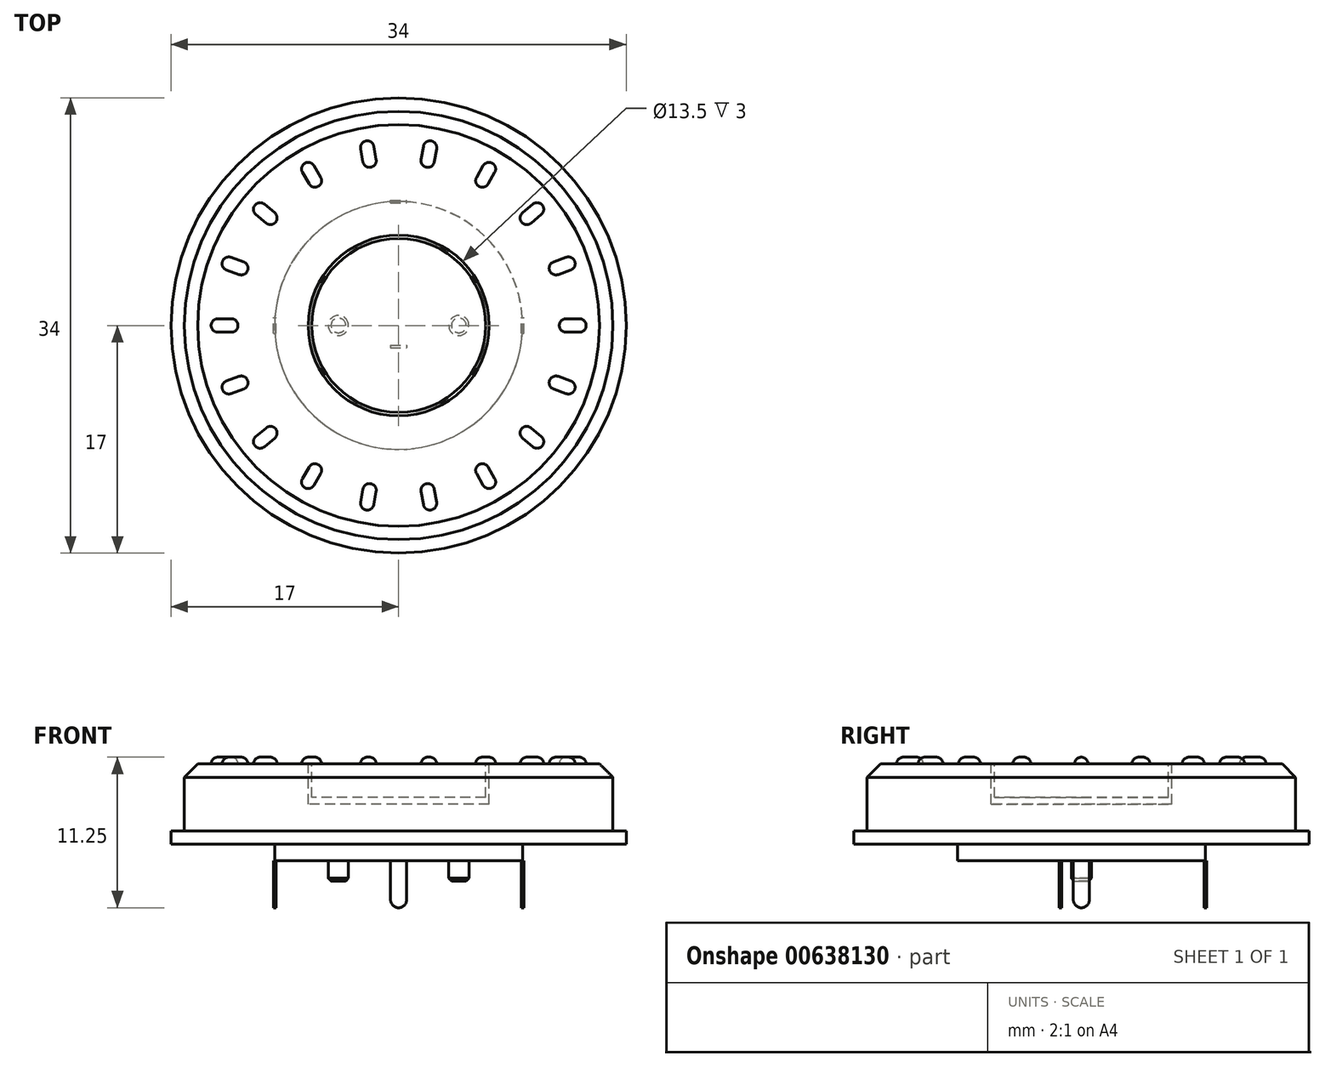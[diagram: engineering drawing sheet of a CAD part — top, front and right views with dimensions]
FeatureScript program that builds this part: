
annotation { "Feature Type Name" : "Feature", "Feature Type Description" : "" }
export const myFeature = defineFeature(function(context is Context, id is Id, definition is map)
    precondition{}
    {
        {
            var Q0;
            Q0=qCreatedBy(makeId("Top.planeOp"),FACE);
            var sketch = newSketch(context, id + "F0", { "sketchPlane" : qUnion([Q0])});
            skCircle(sketch, "E0", {"center": v(0, 0) * mm, "radius": 17 * mm});
            skSolve(sketch);
        }
        {
            var Q0;
            Q0 = qSketchRegion(id + "F0", true);
            extrude(context, id + "F1", {"entities" : qUnion([Q0]), "depth" : 1 * mm, "offsetDistance" : 25 * mm});
        }
        {
            var Q0;
            Q0=makeQuery(id+"F1.opExtrude","CAP_FACE",FACE,{"disambiguationData":[OSD([sQuery(id+"F0.wireOp",EDGE,"E0")])],"isStart":false});
            var sketch = newSketch(context, id + "F2", { "sketchPlane" : qUnion([Q0])});
            skCircle(sketch, "E1", {"center": v(0, 0) * mm, "radius": 16 * mm});
            skSolve(sketch);
        }
        {
            var Q0;
            Q0 = qSketchRegion(id + "F2", true);
            extrude(context, id + "F3", {"entities" : qUnion([Q0]), "operationType" : NewBodyOperationType.ADD, "depth" : 5 * mm, "offsetDistance" : 25 * mm});
        }
        {
            var Q0;
            Q0=makeQuery(id+"F3.opExtrude","CAP_EDGE",EDGE,{"disambiguationData":[OSD([sQuery(id+"F2.wireOp",EDGE,"E1")])],"isStart":false});
            chamfer(context, id + "F4", {"entities" : qUnion([Q0]), "width" : 1 * mm, "tangentPropagation" : true});
        }
        {
            var Q0;
            Q0=makeQuery(id+"F3.opExtrude","CAP_FACE",FACE,{"disambiguationData":[OSD([sQuery(id+"F2.wireOp",EDGE,"E1")])],"isStart":false});
            var sketch = newSketch(context, id + "F5", { "sketchPlane" : qUnion([Q0])});
            skCircle(sketch, "E2", {"center": v(0, 0) * mm, "radius": 6.75 * mm});
            skSolve(sketch);
        }
        {
            var Q0;
            Q0 = qSketchRegion(id + "F5", true);
            extrude(context, id + "F6", {"entities" : qUnion([Q0]), "operationType" : NewBodyOperationType.REMOVE, "oppositeDirection" : true, "depth" : 3 * mm, "offsetDistance" : 25 * mm});
        }
        {
            var Q0;
            Q0=makeQuery(id+"F3.opExtrude","CAP_FACE",FACE,{"disambiguationData":[OSD([sQuery(id+"F2.wireOp",EDGE,"E1")])],"isStart":false});
            var sketch = newSketch(context, id + "F7", { "sketchPlane" : qUnion([Q0])});
            skCircle(sketch, "E3", {"center": v(0, 0) * mm, "radius": 6.5 * mm});
            skSolve(sketch);
        }
        {
            var Q0;
            Q0 = qSketchRegion(id + "F7", true);
            extrude(context, id + "F8", {"entities" : qUnion([Q0]), "oppositeDirection" : true, "depth" : 2.5 * mm, "offsetDistance" : 25 * mm});
        }
        {
            var Q0;
            Q0=makeQuery(id+"F3.opExtrude","CAP_FACE",FACE,{"disambiguationData":[OSD([sQuery(id+"F2.wireOp",EDGE,"E1")])],"isStart":false});
            var sketch = newSketch(context, id + "F9", { "sketchPlane" : qUnion([Q0])});
            skLineSegment(sketch, "E4.bottom", {"start": v(12, 0.5) * mm, "end": v(14, 0.5) * mm});
            skLineSegment(sketch, "E4.top", {"start": v(12, -0.5) * mm, "end": v(14, -0.5) * mm});
            skLineSegment(sketch, "E4.left", {"start": v(12, 0.5) * mm, "end": v(12, -0.5) * mm});
            skLineSegment(sketch, "E4.right", {"start": v(14, 0.5) * mm, "end": v(14, -0.5) * mm});
            skLineSegment(sketch, "E5.1.0", {"start": v(11.1, 4.57) * mm, "end": v(12.98, 5.26) * mm});
            skLineSegment(sketch, "E5.1.1", {"start": v(11.1, 4.57) * mm, "end": v(11.45, 3.63) * mm});
            skLineSegment(sketch, "E5.1.2", {"start": v(11.45, 3.63) * mm, "end": v(13.33, 4.32) * mm});
            skLineSegment(sketch, "E5.1.3", {"start": v(12.98, 5.26) * mm, "end": v(13.33, 4.32) * mm});
            skLineSegment(sketch, "E5.2.0", {"start": v(8.87, 8.1) * mm, "end": v(10.4, 9.38) * mm});
            skLineSegment(sketch, "E5.2.1", {"start": v(8.87, 8.1) * mm, "end": v(9.51, 7.33) * mm});
            skLineSegment(sketch, "E5.2.2", {"start": v(9.51, 7.33) * mm, "end": v(11.05, 8.62) * mm});
            skLineSegment(sketch, "E5.2.3", {"start": v(10.4, 9.38) * mm, "end": v(11.05, 8.62) * mm});
            skLineSegment(sketch, "E5.3.0", {"start": v(5.57, 10.64) * mm, "end": v(6.57, 12.37) * mm});
            skLineSegment(sketch, "E5.3.1", {"start": v(5.57, 10.64) * mm, "end": v(6.43, 10.14) * mm});
            skLineSegment(sketch, "E5.3.2", {"start": v(6.43, 10.14) * mm, "end": v(7.43, 11.87) * mm});
            skLineSegment(sketch, "E5.3.3", {"start": v(6.57, 12.37) * mm, "end": v(7.43, 11.87) * mm});
            skLineSegment(sketch, "E5.4.0", {"start": v(1.6, 11.9) * mm, "end": v(1.94, 13.87) * mm});
            skLineSegment(sketch, "E5.4.1", {"start": v(1.6, 11.9) * mm, "end": v(2.58, 11.73) * mm});
            skLineSegment(sketch, "E5.4.2", {"start": v(2.58, 11.73) * mm, "end": v(2.92, 13.7) * mm});
            skLineSegment(sketch, "E5.4.3", {"start": v(1.94, 13.87) * mm, "end": v(2.92, 13.7) * mm});
            skLineSegment(sketch, "E5.5.0", {"start": v(-2.58, 11.73) * mm, "end": v(-2.92, 13.7) * mm});
            skLineSegment(sketch, "E5.5.1", {"start": v(-2.58, 11.73) * mm, "end": v(-1.6, 11.9) * mm});
            skLineSegment(sketch, "E5.5.2", {"start": v(-1.6, 11.9) * mm, "end": v(-1.94, 13.87) * mm});
            skLineSegment(sketch, "E5.5.3", {"start": v(-2.92, 13.7) * mm, "end": v(-1.94, 13.87) * mm});
            skLineSegment(sketch, "E5.6.0", {"start": v(-6.43, 10.14) * mm, "end": v(-7.43, 11.87) * mm});
            skLineSegment(sketch, "E5.6.1", {"start": v(-6.43, 10.14) * mm, "end": v(-5.57, 10.64) * mm});
            skLineSegment(sketch, "E5.6.2", {"start": v(-5.57, 10.64) * mm, "end": v(-6.57, 12.37) * mm});
            skLineSegment(sketch, "E5.6.3", {"start": v(-7.43, 11.87) * mm, "end": v(-6.57, 12.37) * mm});
            skLineSegment(sketch, "E5.7.0", {"start": v(-9.51, 7.33) * mm, "end": v(-11.05, 8.62) * mm});
            skLineSegment(sketch, "E5.7.1", {"start": v(-9.51, 7.33) * mm, "end": v(-8.87, 8.1) * mm});
            skLineSegment(sketch, "E5.7.2", {"start": v(-8.87, 8.1) * mm, "end": v(-10.4, 9.38) * mm});
            skLineSegment(sketch, "E5.7.3", {"start": v(-11.05, 8.62) * mm, "end": v(-10.4, 9.38) * mm});
            skLineSegment(sketch, "E5.8.0", {"start": v(-11.45, 3.63) * mm, "end": v(-13.33, 4.32) * mm});
            skLineSegment(sketch, "E5.8.1", {"start": v(-11.45, 3.63) * mm, "end": v(-11.1, 4.57) * mm});
            skLineSegment(sketch, "E5.8.2", {"start": v(-11.1, 4.57) * mm, "end": v(-12.98, 5.26) * mm});
            skLineSegment(sketch, "E5.8.3", {"start": v(-13.33, 4.32) * mm, "end": v(-12.98, 5.26) * mm});
            skLineSegment(sketch, "E5.9.0", {"start": v(-12, -0.5) * mm, "end": v(-14, -0.5) * mm});
            skLineSegment(sketch, "E5.9.1", {"start": v(-12, -0.5) * mm, "end": v(-12, 0.5) * mm});
            skLineSegment(sketch, "E5.9.2", {"start": v(-12, 0.5) * mm, "end": v(-14, 0.5) * mm});
            skLineSegment(sketch, "E5.9.3", {"start": v(-14, -0.5) * mm, "end": v(-14, 0.5) * mm});
            skLineSegment(sketch, "E5.10.0", {"start": v(-11.1, -4.57) * mm, "end": v(-12.98, -5.26) * mm});
            skLineSegment(sketch, "E5.10.1", {"start": v(-11.1, -4.57) * mm, "end": v(-11.45, -3.63) * mm});
            skLineSegment(sketch, "E5.10.2", {"start": v(-11.45, -3.63) * mm, "end": v(-13.33, -4.32) * mm});
            skLineSegment(sketch, "E5.10.3", {"start": v(-12.98, -5.26) * mm, "end": v(-13.33, -4.32) * mm});
            skLineSegment(sketch, "E5.11.0", {"start": v(-8.87, -8.1) * mm, "end": v(-10.4, -9.38) * mm});
            skLineSegment(sketch, "E5.11.1", {"start": v(-8.87, -8.1) * mm, "end": v(-9.51, -7.33) * mm});
            skLineSegment(sketch, "E5.11.2", {"start": v(-9.51, -7.33) * mm, "end": v(-11.05, -8.62) * mm});
            skLineSegment(sketch, "E5.11.3", {"start": v(-10.4, -9.38) * mm, "end": v(-11.05, -8.62) * mm});
            skLineSegment(sketch, "E5.12.0", {"start": v(-5.57, -10.64) * mm, "end": v(-6.57, -12.37) * mm});
            skLineSegment(sketch, "E5.12.1", {"start": v(-5.57, -10.64) * mm, "end": v(-6.43, -10.14) * mm});
            skLineSegment(sketch, "E5.12.2", {"start": v(-6.43, -10.14) * mm, "end": v(-7.43, -11.87) * mm});
            skLineSegment(sketch, "E5.12.3", {"start": v(-6.57, -12.37) * mm, "end": v(-7.43, -11.87) * mm});
            skLineSegment(sketch, "E5.13.0", {"start": v(-1.6, -11.9) * mm, "end": v(-1.94, -13.87) * mm});
            skLineSegment(sketch, "E5.13.1", {"start": v(-1.6, -11.9) * mm, "end": v(-2.58, -11.73) * mm});
            skLineSegment(sketch, "E5.13.2", {"start": v(-2.58, -11.73) * mm, "end": v(-2.92, -13.7) * mm});
            skLineSegment(sketch, "E5.13.3", {"start": v(-1.94, -13.87) * mm, "end": v(-2.92, -13.7) * mm});
            skLineSegment(sketch, "E5.14.0", {"start": v(2.58, -11.73) * mm, "end": v(2.92, -13.7) * mm});
            skLineSegment(sketch, "E5.14.1", {"start": v(2.58, -11.73) * mm, "end": v(1.6, -11.9) * mm});
            skLineSegment(sketch, "E5.14.2", {"start": v(1.6, -11.9) * mm, "end": v(1.94, -13.87) * mm});
            skLineSegment(sketch, "E5.14.3", {"start": v(2.92, -13.7) * mm, "end": v(1.94, -13.87) * mm});
            skLineSegment(sketch, "E5.15.0", {"start": v(6.43, -10.14) * mm, "end": v(7.43, -11.87) * mm});
            skLineSegment(sketch, "E5.15.1", {"start": v(6.43, -10.14) * mm, "end": v(5.57, -10.64) * mm});
            skLineSegment(sketch, "E5.15.2", {"start": v(5.57, -10.64) * mm, "end": v(6.57, -12.37) * mm});
            skLineSegment(sketch, "E5.15.3", {"start": v(7.43, -11.87) * mm, "end": v(6.57, -12.37) * mm});
            skLineSegment(sketch, "E5.16.0", {"start": v(9.51, -7.33) * mm, "end": v(11.05, -8.62) * mm});
            skLineSegment(sketch, "E5.16.1", {"start": v(9.51, -7.33) * mm, "end": v(8.87, -8.1) * mm});
            skLineSegment(sketch, "E5.16.2", {"start": v(8.87, -8.1) * mm, "end": v(10.4, -9.38) * mm});
            skLineSegment(sketch, "E5.16.3", {"start": v(11.05, -8.62) * mm, "end": v(10.4, -9.38) * mm});
            skLineSegment(sketch, "E5.17.0", {"start": v(11.45, -3.63) * mm, "end": v(13.33, -4.32) * mm});
            skLineSegment(sketch, "E5.17.1", {"start": v(11.45, -3.63) * mm, "end": v(11.1, -4.57) * mm});
            skLineSegment(sketch, "E5.17.2", {"start": v(11.1, -4.57) * mm, "end": v(12.98, -5.26) * mm});
            skLineSegment(sketch, "E5.17.3", {"start": v(13.33, -4.32) * mm, "end": v(12.98, -5.26) * mm});
            skPoint(sketch, "E5.center", {"position": v(0, 0) * mm});
            skSolve(sketch);
        }
        {
            var Q0;
            Q0=makeQuery(id+"F9.imprint","IMPRINT",FACE,{"disambiguationData":[TD([[makeQuery(id+"F9.imprint","IMPRINT",EDGE,{"derivedFrom":sQuery(id+"F9.wireOp",EDGE,"E4.bottom")}),-1.0]])]});
            var Q1;
            Q1=makeQuery(id+"F9.imprint","IMPRINT",FACE,{"disambiguationData":[TD([[makeQuery(id+"F9.imprint","IMPRINT",EDGE,{"derivedFrom":sQuery(id+"F9.wireOp",EDGE,"E5.1.0")}),-1.0]])]});
            var Q2;
            Q2=makeQuery(id+"F9.imprint","IMPRINT",FACE,{"disambiguationData":[TD([[makeQuery(id+"F9.imprint","IMPRINT",EDGE,{"derivedFrom":sQuery(id+"F9.wireOp",EDGE,"E5.2.0")}),-1.0]])]});
            var Q3;
            Q3=makeQuery(id+"F9.imprint","IMPRINT",FACE,{"disambiguationData":[TD([[makeQuery(id+"F9.imprint","IMPRINT",EDGE,{"derivedFrom":sQuery(id+"F9.wireOp",EDGE,"E5.3.0")}),-1.0]])]});
            var Q4;
            Q4=makeQuery(id+"F9.imprint","IMPRINT",FACE,{"disambiguationData":[TD([[makeQuery(id+"F9.imprint","IMPRINT",EDGE,{"derivedFrom":sQuery(id+"F9.wireOp",EDGE,"E5.4.0")}),-1.0]])]});
            var Q5;
            Q5=makeQuery(id+"F9.imprint","IMPRINT",FACE,{"disambiguationData":[TD([[makeQuery(id+"F9.imprint","IMPRINT",EDGE,{"derivedFrom":sQuery(id+"F9.wireOp",EDGE,"E5.5.0")}),-1.0]])]});
            var Q6;
            Q6=makeQuery(id+"F9.imprint","IMPRINT",FACE,{"disambiguationData":[TD([[makeQuery(id+"F9.imprint","IMPRINT",EDGE,{"derivedFrom":sQuery(id+"F9.wireOp",EDGE,"E5.6.0")}),-1.0]])]});
            var Q7;
            Q7=makeQuery(id+"F9.imprint","IMPRINT",FACE,{"disambiguationData":[TD([[makeQuery(id+"F9.imprint","IMPRINT",EDGE,{"derivedFrom":sQuery(id+"F9.wireOp",EDGE,"E5.7.0")}),-1.0]])]});
            var Q8;
            Q8=makeQuery(id+"F9.imprint","IMPRINT",FACE,{"disambiguationData":[TD([[makeQuery(id+"F9.imprint","IMPRINT",EDGE,{"derivedFrom":sQuery(id+"F9.wireOp",EDGE,"E5.8.0")}),-1.0]])]});
            var Q9;
            Q9=makeQuery(id+"F9.imprint","IMPRINT",FACE,{"disambiguationData":[TD([[makeQuery(id+"F9.imprint","IMPRINT",EDGE,{"derivedFrom":sQuery(id+"F9.wireOp",EDGE,"E5.9.0")}),-1.0]])]});
            var Q10;
            Q10=makeQuery(id+"F9.imprint","IMPRINT",FACE,{"disambiguationData":[TD([[makeQuery(id+"F9.imprint","IMPRINT",EDGE,{"derivedFrom":sQuery(id+"F9.wireOp",EDGE,"E5.10.0")}),-1.0]])]});
            var Q11;
            Q11=makeQuery(id+"F9.imprint","IMPRINT",FACE,{"disambiguationData":[TD([[makeQuery(id+"F9.imprint","IMPRINT",EDGE,{"derivedFrom":sQuery(id+"F9.wireOp",EDGE,"E5.11.0")}),-1.0]])]});
            var Q12;
            Q12=makeQuery(id+"F9.imprint","IMPRINT",FACE,{"disambiguationData":[TD([[makeQuery(id+"F9.imprint","IMPRINT",EDGE,{"derivedFrom":sQuery(id+"F9.wireOp",EDGE,"E5.12.0")}),-1.0]])]});
            var Q13;
            Q13=makeQuery(id+"F9.imprint","IMPRINT",FACE,{"disambiguationData":[TD([[makeQuery(id+"F9.imprint","IMPRINT",EDGE,{"derivedFrom":sQuery(id+"F9.wireOp",EDGE,"E5.13.0")}),-1.0]])]});
            var Q14;
            Q14=makeQuery(id+"F9.imprint","IMPRINT",FACE,{"disambiguationData":[TD([[makeQuery(id+"F9.imprint","IMPRINT",EDGE,{"derivedFrom":sQuery(id+"F9.wireOp",EDGE,"E5.14.0")}),-1.0]])]});
            var Q15;
            Q15=makeQuery(id+"F9.imprint","IMPRINT",FACE,{"disambiguationData":[TD([[makeQuery(id+"F9.imprint","IMPRINT",EDGE,{"derivedFrom":sQuery(id+"F9.wireOp",EDGE,"E5.15.0")}),-1.0]])]});
            var Q16;
            Q16=makeQuery(id+"F9.imprint","IMPRINT",FACE,{"disambiguationData":[TD([[makeQuery(id+"F9.imprint","IMPRINT",EDGE,{"derivedFrom":sQuery(id+"F9.wireOp",EDGE,"E5.16.0")}),-1.0]])]});
            var Q17;
            Q17=makeQuery(id+"F9.imprint","IMPRINT",FACE,{"disambiguationData":[TD([[makeQuery(id+"F9.imprint","IMPRINT",EDGE,{"derivedFrom":sQuery(id+"F9.wireOp",EDGE,"E5.17.0")}),-1.0]])]});
            extrude(context, id + "F10", {"entities" : qUnion([Q0, Q1, Q2, Q3, Q4, Q5, Q6, Q7, Q8, Q9, Q10, Q11, Q12, Q13, Q14, Q15, Q16, Q17]), "operationType" : NewBodyOperationType.ADD, "depth" : 0.5 * mm, "offsetDistance" : 25 * mm});
        }
        {
            var Q0;
            Q0=makeQuery(id+"F10.opExtrude","SWEPT_EDGE",EDGE,{"disambiguationData":[OSD([sQuery(id+"F9.wireOp",EDGE,"E4.top"),sQuery(id+"F9.wireOp",EDGE,"E4.right")])]});
            var Q1;
            Q1=makeQuery(id+"F10.opExtrude","SWEPT_EDGE",EDGE,{"disambiguationData":[OSD([sQuery(id+"F9.wireOp",EDGE,"E4.bottom"),sQuery(id+"F9.wireOp",EDGE,"E4.right")])]});
            var Q2;
            Q2=makeQuery(id+"F10.opExtrude","SWEPT_EDGE",EDGE,{"disambiguationData":[OSD([sQuery(id+"F9.wireOp",EDGE,"E4.top"),sQuery(id+"F9.wireOp",EDGE,"E4.left")])]});
            var Q3;
            Q3=makeQuery(id+"F10.opExtrude","SWEPT_EDGE",EDGE,{"disambiguationData":[OSD([sQuery(id+"F9.wireOp",EDGE,"E4.bottom"),sQuery(id+"F9.wireOp",EDGE,"E4.left")])]});
            var Q4;
            Q4=makeQuery(id+"F10.opExtrude","CAP_EDGE",EDGE,{"disambiguationData":[OSD([sQuery(id+"F9.wireOp",EDGE,"E4.bottom")])],"isStart":false});
            var Q5;
            Q5=makeQuery(id+"F10.opExtrude","CAP_EDGE",EDGE,{"disambiguationData":[OSD([sQuery(id+"F9.wireOp",EDGE,"E4.top")])],"isStart":false});
            var Q6;
            Q6=makeQuery(id+"F10.opExtrude","CAP_EDGE",EDGE,{"disambiguationData":[OSD([sQuery(id+"F9.wireOp",EDGE,"E4.left")])],"isStart":false});
            var Q7;
            Q7=makeQuery(id+"F10.opExtrude","CAP_EDGE",EDGE,{"disambiguationData":[OSD([sQuery(id+"F9.wireOp",EDGE,"E4.right")])],"isStart":false});
            fillet(context, id + "F11", {"entities" : qUnion([Q0, Q1, Q2, Q3, Q4, Q5, Q6, Q7]), "radius" : 0.5 * mm, "tangentPropagation" : true, "allowEdgeOverflow" : false});
        }
        {
            var Q0;
            Q0=makeQuery(id+"F10.opExtrude","SWEPT_EDGE",EDGE,{"disambiguationData":[OSD([sQuery(id+"F9.wireOp",EDGE,"E5.1.0"),sQuery(id+"F9.wireOp",EDGE,"E5.1.3")])]});
            var Q1;
            Q1=makeQuery(id+"F10.opExtrude","SWEPT_EDGE",EDGE,{"disambiguationData":[OSD([sQuery(id+"F9.wireOp",EDGE,"E5.1.2"),sQuery(id+"F9.wireOp",EDGE,"E5.1.3")])]});
            var Q2;
            Q2=makeQuery(id+"F10.opExtrude","SWEPT_EDGE",EDGE,{"disambiguationData":[OSD([sQuery(id+"F9.wireOp",EDGE,"E5.1.0"),sQuery(id+"F9.wireOp",EDGE,"E5.1.1")])]});
            var Q3;
            Q3=makeQuery(id+"F10.opExtrude","SWEPT_EDGE",EDGE,{"disambiguationData":[OSD([sQuery(id+"F9.wireOp",EDGE,"E5.1.1"),sQuery(id+"F9.wireOp",EDGE,"E5.1.2")])]});
            var Q4;
            Q4=makeQuery(id+"F10.opExtrude","CAP_EDGE",EDGE,{"disambiguationData":[OSD([sQuery(id+"F9.wireOp",EDGE,"E5.1.2")])],"isStart":false});
            var Q5;
            Q5=makeQuery(id+"F10.opExtrude","CAP_EDGE",EDGE,{"disambiguationData":[OSD([sQuery(id+"F9.wireOp",EDGE,"E5.1.0")])],"isStart":false});
            var Q6;
            Q6=makeQuery(id+"F10.opExtrude","CAP_EDGE",EDGE,{"disambiguationData":[OSD([sQuery(id+"F9.wireOp",EDGE,"E5.1.1")])],"isStart":false});
            var Q7;
            Q7=makeQuery(id+"F10.opExtrude","CAP_EDGE",EDGE,{"disambiguationData":[OSD([sQuery(id+"F9.wireOp",EDGE,"E5.1.3")])],"isStart":false});
            fillet(context, id + "F12", {"entities" : qUnion([Q0, Q1, Q2, Q3, Q4, Q5, Q6, Q7]), "radius" : 0.5 * mm, "tangentPropagation" : true, "allowEdgeOverflow" : false});
        }
        {
            var Q0;
            Q0=makeQuery(id+"F10.opExtrude","SWEPT_EDGE",EDGE,{"disambiguationData":[OSD([sQuery(id+"F9.wireOp",EDGE,"E5.17.2"),sQuery(id+"F9.wireOp",EDGE,"E5.17.3")])]});
            var Q1;
            Q1=makeQuery(id+"F10.opExtrude","SWEPT_EDGE",EDGE,{"disambiguationData":[OSD([sQuery(id+"F9.wireOp",EDGE,"E5.17.0"),sQuery(id+"F9.wireOp",EDGE,"E5.17.3")])]});
            var Q2;
            Q2=makeQuery(id+"F10.opExtrude","SWEPT_EDGE",EDGE,{"disambiguationData":[OSD([sQuery(id+"F9.wireOp",EDGE,"E5.17.1"),sQuery(id+"F9.wireOp",EDGE,"E5.17.2")])]});
            var Q3;
            Q3=makeQuery(id+"F10.opExtrude","SWEPT_EDGE",EDGE,{"disambiguationData":[OSD([sQuery(id+"F9.wireOp",EDGE,"E5.17.0"),sQuery(id+"F9.wireOp",EDGE,"E5.17.1")])]});
            var Q4;
            Q4=makeQuery(id+"F10.opExtrude","CAP_EDGE",EDGE,{"disambiguationData":[OSD([sQuery(id+"F9.wireOp",EDGE,"E5.17.0")])],"isStart":false});
            var Q5;
            Q5=makeQuery(id+"F10.opExtrude","CAP_EDGE",EDGE,{"disambiguationData":[OSD([sQuery(id+"F9.wireOp",EDGE,"E5.17.2")])],"isStart":false});
            var Q6;
            Q6=makeQuery(id+"F10.opExtrude","CAP_EDGE",EDGE,{"disambiguationData":[OSD([sQuery(id+"F9.wireOp",EDGE,"E5.17.3")])],"isStart":false});
            var Q7;
            Q7=makeQuery(id+"F10.opExtrude","CAP_FACE",FACE,{"disambiguationData":[OSD([sQuery(id+"F9.wireOp",EDGE,"E5.17.0"),sQuery(id+"F9.wireOp",EDGE,"E5.17.1"),sQuery(id+"F9.wireOp",EDGE,"E5.17.2"),sQuery(id+"F9.wireOp",EDGE,"E5.17.3")])],"isStart":false});
            fillet(context, id + "F13", {"entities" : qUnion([Q0, Q1, Q2, Q3, Q4, Q5, Q6, Q7]), "radius" : 0.5 * mm, "tangentPropagation" : true, "allowEdgeOverflow" : false});
        }
        {
            var Q0;
            Q0=makeQuery(id+"F10.opExtrude","SWEPT_EDGE",EDGE,{"disambiguationData":[OSD([sQuery(id+"F9.wireOp",EDGE,"E5.16.2"),sQuery(id+"F9.wireOp",EDGE,"E5.16.3")])]});
            var Q1;
            Q1=makeQuery(id+"F10.opExtrude","SWEPT_EDGE",EDGE,{"disambiguationData":[OSD([sQuery(id+"F9.wireOp",EDGE,"E5.16.0"),sQuery(id+"F9.wireOp",EDGE,"E5.16.3")])]});
            var Q2;
            Q2=makeQuery(id+"F10.opExtrude","SWEPT_EDGE",EDGE,{"disambiguationData":[OSD([sQuery(id+"F9.wireOp",EDGE,"E5.16.1"),sQuery(id+"F9.wireOp",EDGE,"E5.16.2")])]});
            var Q3;
            Q3=makeQuery(id+"F10.opExtrude","SWEPT_EDGE",EDGE,{"disambiguationData":[OSD([sQuery(id+"F9.wireOp",EDGE,"E5.16.0"),sQuery(id+"F9.wireOp",EDGE,"E5.16.1")])]});
            var Q4;
            Q4=makeQuery(id+"F10.opExtrude","CAP_EDGE",EDGE,{"disambiguationData":[OSD([sQuery(id+"F9.wireOp",EDGE,"E5.16.0")])],"isStart":false});
            var Q5;
            Q5=makeQuery(id+"F10.opExtrude","CAP_EDGE",EDGE,{"disambiguationData":[OSD([sQuery(id+"F9.wireOp",EDGE,"E5.16.2")])],"isStart":false});
            var Q6;
            Q6=makeQuery(id+"F10.opExtrude","CAP_EDGE",EDGE,{"disambiguationData":[OSD([sQuery(id+"F9.wireOp",EDGE,"E5.16.3")])],"isStart":false});
            var Q7;
            Q7=makeQuery(id+"F10.opExtrude","CAP_EDGE",EDGE,{"disambiguationData":[OSD([sQuery(id+"F9.wireOp",EDGE,"E5.16.1")])],"isStart":false});
            fillet(context, id + "F14", {"entities" : qUnion([Q0, Q1, Q2, Q3, Q4, Q5, Q6, Q7]), "radius" : 0.5 * mm, "tangentPropagation" : true, "allowEdgeOverflow" : false});
        }
        {
            var Q0;
            Q0=makeQuery(id+"F10.opExtrude","SWEPT_EDGE",EDGE,{"disambiguationData":[OSD([sQuery(id+"F9.wireOp",EDGE,"E5.15.0"),sQuery(id+"F9.wireOp",EDGE,"E5.15.3")])]});
            var Q1;
            Q1=makeQuery(id+"F10.opExtrude","SWEPT_EDGE",EDGE,{"disambiguationData":[OSD([sQuery(id+"F9.wireOp",EDGE,"E5.15.0"),sQuery(id+"F9.wireOp",EDGE,"E5.15.1")])]});
            var Q2;
            Q2=makeQuery(id+"F10.opExtrude","SWEPT_EDGE",EDGE,{"disambiguationData":[OSD([sQuery(id+"F9.wireOp",EDGE,"E5.15.2"),sQuery(id+"F9.wireOp",EDGE,"E5.15.3")])]});
            var Q3;
            Q3=makeQuery(id+"F10.opExtrude","SWEPT_EDGE",EDGE,{"disambiguationData":[OSD([sQuery(id+"F9.wireOp",EDGE,"E5.15.1"),sQuery(id+"F9.wireOp",EDGE,"E5.15.2")])]});
            var Q4;
            Q4=makeQuery(id+"F10.opExtrude","CAP_EDGE",EDGE,{"disambiguationData":[OSD([sQuery(id+"F9.wireOp",EDGE,"E5.15.2")])],"isStart":false});
            var Q5;
            Q5=makeQuery(id+"F10.opExtrude","CAP_EDGE",EDGE,{"disambiguationData":[OSD([sQuery(id+"F9.wireOp",EDGE,"E5.15.0")])],"isStart":false});
            var Q6;
            Q6=makeQuery(id+"F10.opExtrude","CAP_EDGE",EDGE,{"disambiguationData":[OSD([sQuery(id+"F9.wireOp",EDGE,"E5.15.3")])],"isStart":false});
            var Q7;
            Q7=makeQuery(id+"F10.opExtrude","CAP_EDGE",EDGE,{"disambiguationData":[OSD([sQuery(id+"F9.wireOp",EDGE,"E5.15.1")])],"isStart":false});
            fillet(context, id + "F15", {"entities" : qUnion([Q0, Q1, Q2, Q3, Q4, Q5, Q6, Q7]), "radius" : 0.5 * mm, "tangentPropagation" : true, "allowEdgeOverflow" : false});
        }
        {
            var Q0;
            Q0=makeQuery(id+"F10.opExtrude","SWEPT_EDGE",EDGE,{"disambiguationData":[OSD([sQuery(id+"F9.wireOp",EDGE,"E5.14.1"),sQuery(id+"F9.wireOp",EDGE,"E5.14.2")])]});
            var Q1;
            Q1=makeQuery(id+"F10.opExtrude","SWEPT_EDGE",EDGE,{"disambiguationData":[OSD([sQuery(id+"F9.wireOp",EDGE,"E5.14.2"),sQuery(id+"F9.wireOp",EDGE,"E5.14.3")])]});
            var Q2;
            Q2=makeQuery(id+"F10.opExtrude","SWEPT_EDGE",EDGE,{"disambiguationData":[OSD([sQuery(id+"F9.wireOp",EDGE,"E5.14.0"),sQuery(id+"F9.wireOp",EDGE,"E5.14.3")])]});
            var Q3;
            Q3=makeQuery(id+"F10.opExtrude","SWEPT_EDGE",EDGE,{"disambiguationData":[OSD([sQuery(id+"F9.wireOp",EDGE,"E5.14.0"),sQuery(id+"F9.wireOp",EDGE,"E5.14.1")])]});
            var Q4;
            Q4=makeQuery(id+"F10.opExtrude","CAP_EDGE",EDGE,{"disambiguationData":[OSD([sQuery(id+"F9.wireOp",EDGE,"E5.14.2")])],"isStart":false});
            var Q5;
            Q5=makeQuery(id+"F10.opExtrude","CAP_EDGE",EDGE,{"disambiguationData":[OSD([sQuery(id+"F9.wireOp",EDGE,"E5.14.0")])],"isStart":false});
            var Q6;
            Q6=makeQuery(id+"F10.opExtrude","CAP_EDGE",EDGE,{"disambiguationData":[OSD([sQuery(id+"F9.wireOp",EDGE,"E5.14.3")])],"isStart":false});
            var Q7;
            Q7=makeQuery(id+"F10.opExtrude","CAP_EDGE",EDGE,{"disambiguationData":[OSD([sQuery(id+"F9.wireOp",EDGE,"E5.14.1")])],"isStart":false});
            fillet(context, id + "F16", {"entities" : qUnion([Q0, Q1, Q2, Q3, Q4, Q5, Q6, Q7]), "radius" : 0.5 * mm, "tangentPropagation" : true, "allowEdgeOverflow" : false});
        }
        {
            var Q0;
            Q0=makeQuery(id+"F10.opExtrude","SWEPT_EDGE",EDGE,{"disambiguationData":[OSD([sQuery(id+"F9.wireOp",EDGE,"E5.13.2"),sQuery(id+"F9.wireOp",EDGE,"E5.13.3")])]});
            var Q1;
            Q1=makeQuery(id+"F10.opExtrude","SWEPT_EDGE",EDGE,{"disambiguationData":[OSD([sQuery(id+"F9.wireOp",EDGE,"E5.13.0"),sQuery(id+"F9.wireOp",EDGE,"E5.13.3")])]});
            var Q2;
            Q2=makeQuery(id+"F10.opExtrude","SWEPT_EDGE",EDGE,{"disambiguationData":[OSD([sQuery(id+"F9.wireOp",EDGE,"E5.13.1"),sQuery(id+"F9.wireOp",EDGE,"E5.13.2")])]});
            var Q3;
            Q3=makeQuery(id+"F10.opExtrude","SWEPT_EDGE",EDGE,{"disambiguationData":[OSD([sQuery(id+"F9.wireOp",EDGE,"E5.13.0"),sQuery(id+"F9.wireOp",EDGE,"E5.13.1")])]});
            var Q4;
            Q4=makeQuery(id+"F10.opExtrude","CAP_EDGE",EDGE,{"disambiguationData":[OSD([sQuery(id+"F9.wireOp",EDGE,"E5.13.0")])],"isStart":false});
            var Q5;
            Q5=makeQuery(id+"F10.opExtrude","CAP_EDGE",EDGE,{"disambiguationData":[OSD([sQuery(id+"F9.wireOp",EDGE,"E5.13.2")])],"isStart":false});
            var Q6;
            Q6=makeQuery(id+"F10.opExtrude","CAP_EDGE",EDGE,{"disambiguationData":[OSD([sQuery(id+"F9.wireOp",EDGE,"E5.13.3")])],"isStart":false});
            var Q7;
            Q7=makeQuery(id+"F10.opExtrude","CAP_EDGE",EDGE,{"disambiguationData":[OSD([sQuery(id+"F9.wireOp",EDGE,"E5.13.1")])],"isStart":false});
            fillet(context, id + "F17", {"entities" : qUnion([Q0, Q1, Q2, Q3, Q4, Q5, Q6, Q7]), "radius" : 0.5 * mm, "tangentPropagation" : true, "allowEdgeOverflow" : false});
        }
        {
            var Q0;
            Q0=makeQuery(id+"F10.opExtrude","SWEPT_EDGE",EDGE,{"disambiguationData":[OSD([sQuery(id+"F9.wireOp",EDGE,"E5.12.2"),sQuery(id+"F9.wireOp",EDGE,"E5.12.3")])]});
            var Q1;
            Q1=makeQuery(id+"F10.opExtrude","SWEPT_EDGE",EDGE,{"disambiguationData":[OSD([sQuery(id+"F9.wireOp",EDGE,"E5.12.0"),sQuery(id+"F9.wireOp",EDGE,"E5.12.3")])]});
            var Q2;
            Q2=makeQuery(id+"F10.opExtrude","SWEPT_EDGE",EDGE,{"disambiguationData":[OSD([sQuery(id+"F9.wireOp",EDGE,"E5.12.1"),sQuery(id+"F9.wireOp",EDGE,"E5.12.2")])]});
            var Q3;
            Q3=makeQuery(id+"F10.opExtrude","SWEPT_EDGE",EDGE,{"disambiguationData":[OSD([sQuery(id+"F9.wireOp",EDGE,"E5.12.0"),sQuery(id+"F9.wireOp",EDGE,"E5.12.1")])]});
            var Q4;
            Q4=makeQuery(id+"F10.opExtrude","CAP_EDGE",EDGE,{"disambiguationData":[OSD([sQuery(id+"F9.wireOp",EDGE,"E5.12.2")])],"isStart":false});
            var Q5;
            Q5=makeQuery(id+"F10.opExtrude","CAP_EDGE",EDGE,{"disambiguationData":[OSD([sQuery(id+"F9.wireOp",EDGE,"E5.12.0")])],"isStart":false});
            var Q6;
            Q6=makeQuery(id+"F10.opExtrude","CAP_EDGE",EDGE,{"disambiguationData":[OSD([sQuery(id+"F9.wireOp",EDGE,"E5.12.3")])],"isStart":false});
            var Q7;
            Q7=makeQuery(id+"F10.opExtrude","CAP_EDGE",EDGE,{"disambiguationData":[OSD([sQuery(id+"F9.wireOp",EDGE,"E5.12.1")])],"isStart":false});
            fillet(context, id + "F18", {"entities" : qUnion([Q0, Q1, Q2, Q3, Q4, Q5, Q6, Q7]), "radius" : 0.5 * mm, "tangentPropagation" : true, "allowEdgeOverflow" : false});
        }
        {
            var Q0;
            Q0=makeQuery(id+"F10.opExtrude","SWEPT_EDGE",EDGE,{"disambiguationData":[OSD([sQuery(id+"F9.wireOp",EDGE,"E5.11.2"),sQuery(id+"F9.wireOp",EDGE,"E5.11.3")])]});
            var Q1;
            Q1=makeQuery(id+"F10.opExtrude","SWEPT_EDGE",EDGE,{"disambiguationData":[OSD([sQuery(id+"F9.wireOp",EDGE,"E5.11.0"),sQuery(id+"F9.wireOp",EDGE,"E5.11.3")])]});
            var Q2;
            Q2=makeQuery(id+"F10.opExtrude","SWEPT_EDGE",EDGE,{"disambiguationData":[OSD([sQuery(id+"F9.wireOp",EDGE,"E5.11.1"),sQuery(id+"F9.wireOp",EDGE,"E5.11.2")])]});
            var Q3;
            Q3=makeQuery(id+"F10.opExtrude","SWEPT_EDGE",EDGE,{"disambiguationData":[OSD([sQuery(id+"F9.wireOp",EDGE,"E5.11.0"),sQuery(id+"F9.wireOp",EDGE,"E5.11.1")])]});
            var Q4;
            Q4=makeQuery(id+"F10.opExtrude","CAP_EDGE",EDGE,{"disambiguationData":[OSD([sQuery(id+"F9.wireOp",EDGE,"E5.11.0")])],"isStart":false});
            var Q5;
            Q5=makeQuery(id+"F10.opExtrude","CAP_EDGE",EDGE,{"disambiguationData":[OSD([sQuery(id+"F9.wireOp",EDGE,"E5.11.2")])],"isStart":false});
            var Q6;
            Q6=makeQuery(id+"F10.opExtrude","CAP_EDGE",EDGE,{"disambiguationData":[OSD([sQuery(id+"F9.wireOp",EDGE,"E5.11.1")])],"isStart":false});
            var Q7;
            Q7=makeQuery(id+"F10.opExtrude","CAP_EDGE",EDGE,{"disambiguationData":[OSD([sQuery(id+"F9.wireOp",EDGE,"E5.11.3")])],"isStart":false});
            fillet(context, id + "F19", {"entities" : qUnion([Q0, Q1, Q2, Q3, Q4, Q5, Q6, Q7]), "radius" : 0.5 * mm, "tangentPropagation" : true, "allowEdgeOverflow" : false});
        }
        {
            var Q0;
            Q0=makeQuery(id+"F10.opExtrude","SWEPT_EDGE",EDGE,{"disambiguationData":[OSD([sQuery(id+"F9.wireOp",EDGE,"E5.10.2"),sQuery(id+"F9.wireOp",EDGE,"E5.10.3")])]});
            var Q1;
            Q1=makeQuery(id+"F10.opExtrude","SWEPT_EDGE",EDGE,{"disambiguationData":[OSD([sQuery(id+"F9.wireOp",EDGE,"E5.10.0"),sQuery(id+"F9.wireOp",EDGE,"E5.10.3")])]});
            var Q2;
            Q2=makeQuery(id+"F10.opExtrude","SWEPT_EDGE",EDGE,{"disambiguationData":[OSD([sQuery(id+"F9.wireOp",EDGE,"E5.10.1"),sQuery(id+"F9.wireOp",EDGE,"E5.10.2")])]});
            var Q3;
            Q3=makeQuery(id+"F10.opExtrude","SWEPT_EDGE",EDGE,{"disambiguationData":[OSD([sQuery(id+"F9.wireOp",EDGE,"E5.10.0"),sQuery(id+"F9.wireOp",EDGE,"E5.10.1")])]});
            var Q4;
            Q4=makeQuery(id+"F10.opExtrude","CAP_EDGE",EDGE,{"disambiguationData":[OSD([sQuery(id+"F9.wireOp",EDGE,"E5.10.0")])],"isStart":false});
            var Q5;
            Q5=makeQuery(id+"F10.opExtrude","CAP_EDGE",EDGE,{"disambiguationData":[OSD([sQuery(id+"F9.wireOp",EDGE,"E5.10.2")])],"isStart":false});
            var Q6;
            Q6=makeQuery(id+"F10.opExtrude","CAP_EDGE",EDGE,{"disambiguationData":[OSD([sQuery(id+"F9.wireOp",EDGE,"E5.10.1")])],"isStart":false});
            var Q7;
            Q7=makeQuery(id+"F10.opExtrude","CAP_EDGE",EDGE,{"disambiguationData":[OSD([sQuery(id+"F9.wireOp",EDGE,"E5.10.3")])],"isStart":false});
            fillet(context, id + "F20", {"entities" : qUnion([Q0, Q1, Q2, Q3, Q4, Q5, Q6, Q7]), "radius" : 0.5 * mm, "tangentPropagation" : true, "allowEdgeOverflow" : false});
        }
        {
            var Q0;
            Q0=makeQuery(id+"F10.opExtrude","SWEPT_EDGE",EDGE,{"disambiguationData":[OSD([sQuery(id+"F9.wireOp",EDGE,"E5.9.2"),sQuery(id+"F9.wireOp",EDGE,"E5.9.3")])]});
            var Q1;
            Q1=makeQuery(id+"F10.opExtrude","SWEPT_EDGE",EDGE,{"disambiguationData":[OSD([sQuery(id+"F9.wireOp",EDGE,"E5.9.0"),sQuery(id+"F9.wireOp",EDGE,"E5.9.3")])]});
            var Q2;
            Q2=makeQuery(id+"F10.opExtrude","SWEPT_EDGE",EDGE,{"disambiguationData":[OSD([sQuery(id+"F9.wireOp",EDGE,"E5.9.1"),sQuery(id+"F9.wireOp",EDGE,"E5.9.2")])]});
            var Q3;
            Q3=makeQuery(id+"F10.opExtrude","SWEPT_EDGE",EDGE,{"disambiguationData":[OSD([sQuery(id+"F9.wireOp",EDGE,"E5.9.0"),sQuery(id+"F9.wireOp",EDGE,"E5.9.1")])]});
            var Q4;
            Q4=makeQuery(id+"F10.opExtrude","CAP_EDGE",EDGE,{"disambiguationData":[OSD([sQuery(id+"F9.wireOp",EDGE,"E5.9.0")])],"isStart":false});
            var Q5;
            Q5=makeQuery(id+"F10.opExtrude","CAP_EDGE",EDGE,{"disambiguationData":[OSD([sQuery(id+"F9.wireOp",EDGE,"E5.9.2")])],"isStart":false});
            var Q6;
            Q6=makeQuery(id+"F10.opExtrude","CAP_EDGE",EDGE,{"disambiguationData":[OSD([sQuery(id+"F9.wireOp",EDGE,"E5.9.1")])],"isStart":false});
            var Q7;
            Q7=makeQuery(id+"F10.opExtrude","CAP_EDGE",EDGE,{"disambiguationData":[OSD([sQuery(id+"F9.wireOp",EDGE,"E5.9.3")])],"isStart":false});
            fillet(context, id + "F21", {"entities" : qUnion([Q0, Q1, Q2, Q3, Q4, Q5, Q6, Q7]), "radius" : 0.5 * mm, "tangentPropagation" : true, "allowEdgeOverflow" : false});
        }
        {
            var Q0;
            Q0=makeQuery(id+"F10.opExtrude","SWEPT_EDGE",EDGE,{"disambiguationData":[OSD([sQuery(id+"F9.wireOp",EDGE,"E5.8.0"),sQuery(id+"F9.wireOp",EDGE,"E5.8.3")])]});
            var Q1;
            Q1=makeQuery(id+"F10.opExtrude","SWEPT_EDGE",EDGE,{"disambiguationData":[OSD([sQuery(id+"F9.wireOp",EDGE,"E5.8.2"),sQuery(id+"F9.wireOp",EDGE,"E5.8.3")])]});
            var Q2;
            Q2=makeQuery(id+"F10.opExtrude","SWEPT_EDGE",EDGE,{"disambiguationData":[OSD([sQuery(id+"F9.wireOp",EDGE,"E5.8.0"),sQuery(id+"F9.wireOp",EDGE,"E5.8.1")])]});
            var Q3;
            Q3=makeQuery(id+"F10.opExtrude","SWEPT_EDGE",EDGE,{"disambiguationData":[OSD([sQuery(id+"F9.wireOp",EDGE,"E5.8.1"),sQuery(id+"F9.wireOp",EDGE,"E5.8.2")])]});
            var Q4;
            Q4=makeQuery(id+"F10.opExtrude","CAP_EDGE",EDGE,{"disambiguationData":[OSD([sQuery(id+"F9.wireOp",EDGE,"E5.8.0")])],"isStart":false});
            var Q5;
            Q5=makeQuery(id+"F10.opExtrude","CAP_EDGE",EDGE,{"disambiguationData":[OSD([sQuery(id+"F9.wireOp",EDGE,"E5.8.2")])],"isStart":false});
            var Q6;
            Q6=makeQuery(id+"F10.opExtrude","CAP_EDGE",EDGE,{"disambiguationData":[OSD([sQuery(id+"F9.wireOp",EDGE,"E5.8.1")])],"isStart":false});
            var Q7;
            Q7=makeQuery(id+"F10.opExtrude","CAP_EDGE",EDGE,{"disambiguationData":[OSD([sQuery(id+"F9.wireOp",EDGE,"E5.8.3")])],"isStart":false});
            fillet(context, id + "F22", {"entities" : qUnion([Q0, Q1, Q2, Q3, Q4, Q5, Q6, Q7]), "radius" : 0.5 * mm, "tangentPropagation" : true, "allowEdgeOverflow" : false});
        }
        {
            var Q0;
            Q0=makeQuery(id+"F10.opExtrude","SWEPT_EDGE",EDGE,{"disambiguationData":[OSD([sQuery(id+"F9.wireOp",EDGE,"E5.7.0"),sQuery(id+"F9.wireOp",EDGE,"E5.7.3")])]});
            var Q1;
            Q1=makeQuery(id+"F10.opExtrude","SWEPT_EDGE",EDGE,{"disambiguationData":[OSD([sQuery(id+"F9.wireOp",EDGE,"E5.7.2"),sQuery(id+"F9.wireOp",EDGE,"E5.7.3")])]});
            var Q2;
            Q2=makeQuery(id+"F10.opExtrude","SWEPT_EDGE",EDGE,{"disambiguationData":[OSD([sQuery(id+"F9.wireOp",EDGE,"E5.7.0"),sQuery(id+"F9.wireOp",EDGE,"E5.7.1")])]});
            var Q3;
            Q3=makeQuery(id+"F10.opExtrude","SWEPT_EDGE",EDGE,{"disambiguationData":[OSD([sQuery(id+"F9.wireOp",EDGE,"E5.7.1"),sQuery(id+"F9.wireOp",EDGE,"E5.7.2")])]});
            var Q4;
            Q4=makeQuery(id+"F10.opExtrude","CAP_EDGE",EDGE,{"disambiguationData":[OSD([sQuery(id+"F9.wireOp",EDGE,"E5.7.0")])],"isStart":false});
            var Q5;
            Q5=makeQuery(id+"F10.opExtrude","CAP_EDGE",EDGE,{"disambiguationData":[OSD([sQuery(id+"F9.wireOp",EDGE,"E5.7.2")])],"isStart":false});
            var Q6;
            Q6=makeQuery(id+"F10.opExtrude","CAP_EDGE",EDGE,{"disambiguationData":[OSD([sQuery(id+"F9.wireOp",EDGE,"E5.7.1")])],"isStart":false});
            var Q7;
            Q7=makeQuery(id+"F10.opExtrude","CAP_EDGE",EDGE,{"disambiguationData":[OSD([sQuery(id+"F9.wireOp",EDGE,"E5.7.3")])],"isStart":false});
            fillet(context, id + "F23", {"entities" : qUnion([Q0, Q1, Q2, Q3, Q4, Q5, Q6, Q7]), "radius" : 0.5 * mm, "tangentPropagation" : true, "allowEdgeOverflow" : false});
        }
        {
            var Q0;
            Q0=makeQuery(id+"F10.opExtrude","SWEPT_EDGE",EDGE,{"disambiguationData":[OSD([sQuery(id+"F9.wireOp",EDGE,"E5.6.0"),sQuery(id+"F9.wireOp",EDGE,"E5.6.3")])]});
            var Q1;
            Q1=makeQuery(id+"F10.opExtrude","SWEPT_EDGE",EDGE,{"disambiguationData":[OSD([sQuery(id+"F9.wireOp",EDGE,"E5.6.0"),sQuery(id+"F9.wireOp",EDGE,"E5.6.1")])]});
            var Q2;
            Q2=makeQuery(id+"F10.opExtrude","SWEPT_EDGE",EDGE,{"disambiguationData":[OSD([sQuery(id+"F9.wireOp",EDGE,"E5.6.2"),sQuery(id+"F9.wireOp",EDGE,"E5.6.3")])]});
            var Q3;
            Q3=makeQuery(id+"F10.opExtrude","SWEPT_EDGE",EDGE,{"disambiguationData":[OSD([sQuery(id+"F9.wireOp",EDGE,"E5.6.1"),sQuery(id+"F9.wireOp",EDGE,"E5.6.2")])]});
            var Q4;
            Q4=makeQuery(id+"F10.opExtrude","CAP_EDGE",EDGE,{"disambiguationData":[OSD([sQuery(id+"F9.wireOp",EDGE,"E5.6.2")])],"isStart":false});
            var Q5;
            Q5=makeQuery(id+"F10.opExtrude","CAP_EDGE",EDGE,{"disambiguationData":[OSD([sQuery(id+"F9.wireOp",EDGE,"E5.6.0")])],"isStart":false});
            var Q6;
            Q6=makeQuery(id+"F10.opExtrude","CAP_EDGE",EDGE,{"disambiguationData":[OSD([sQuery(id+"F9.wireOp",EDGE,"E5.6.1")])],"isStart":false});
            var Q7;
            Q7=makeQuery(id+"F10.opExtrude","CAP_EDGE",EDGE,{"disambiguationData":[OSD([sQuery(id+"F9.wireOp",EDGE,"E5.6.3")])],"isStart":false});
            fillet(context, id + "F24", {"entities" : qUnion([Q0, Q1, Q2, Q3, Q4, Q5, Q6, Q7]), "radius" : 0.5 * mm, "tangentPropagation" : true, "allowEdgeOverflow" : false});
        }
        {
            var Q0;
            Q0=makeQuery(id+"F10.opExtrude","SWEPT_EDGE",EDGE,{"disambiguationData":[OSD([sQuery(id+"F9.wireOp",EDGE,"E5.5.0"),sQuery(id+"F9.wireOp",EDGE,"E5.5.3")])]});
            var Q1;
            Q1=makeQuery(id+"F10.opExtrude","SWEPT_EDGE",EDGE,{"disambiguationData":[OSD([sQuery(id+"F9.wireOp",EDGE,"E5.5.0"),sQuery(id+"F9.wireOp",EDGE,"E5.5.1")])]});
            var Q2;
            Q2=makeQuery(id+"F10.opExtrude","SWEPT_EDGE",EDGE,{"disambiguationData":[OSD([sQuery(id+"F9.wireOp",EDGE,"E5.5.1"),sQuery(id+"F9.wireOp",EDGE,"E5.5.2")])]});
            var Q3;
            Q3=makeQuery(id+"F10.opExtrude","SWEPT_EDGE",EDGE,{"disambiguationData":[OSD([sQuery(id+"F9.wireOp",EDGE,"E5.5.2"),sQuery(id+"F9.wireOp",EDGE,"E5.5.3")])]});
            var Q4;
            Q4=makeQuery(id+"F10.opExtrude","CAP_EDGE",EDGE,{"disambiguationData":[OSD([sQuery(id+"F9.wireOp",EDGE,"E5.5.2")])],"isStart":false});
            var Q5;
            Q5=makeQuery(id+"F10.opExtrude","CAP_EDGE",EDGE,{"disambiguationData":[OSD([sQuery(id+"F9.wireOp",EDGE,"E5.5.0")])],"isStart":false});
            var Q6;
            Q6=makeQuery(id+"F10.opExtrude","CAP_EDGE",EDGE,{"disambiguationData":[OSD([sQuery(id+"F9.wireOp",EDGE,"E5.5.1")])],"isStart":false});
            var Q7;
            Q7=makeQuery(id+"F10.opExtrude","CAP_EDGE",EDGE,{"disambiguationData":[OSD([sQuery(id+"F9.wireOp",EDGE,"E5.5.3")])],"isStart":false});
            fillet(context, id + "F25", {"entities" : qUnion([Q0, Q1, Q2, Q3, Q4, Q5, Q6, Q7]), "radius" : 0.5 * mm, "tangentPropagation" : true, "allowEdgeOverflow" : false});
        }
        {
            var Q0;
            Q0=makeQuery(id+"F10.opExtrude","SWEPT_EDGE",EDGE,{"disambiguationData":[OSD([sQuery(id+"F9.wireOp",EDGE,"E5.4.0"),sQuery(id+"F9.wireOp",EDGE,"E5.4.3")])]});
            var Q1;
            Q1=makeQuery(id+"F10.opExtrude","SWEPT_EDGE",EDGE,{"disambiguationData":[OSD([sQuery(id+"F9.wireOp",EDGE,"E5.4.0"),sQuery(id+"F9.wireOp",EDGE,"E5.4.1")])]});
            var Q2;
            Q2=makeQuery(id+"F10.opExtrude","SWEPT_EDGE",EDGE,{"disambiguationData":[OSD([sQuery(id+"F9.wireOp",EDGE,"E5.4.1"),sQuery(id+"F9.wireOp",EDGE,"E5.4.2")])]});
            var Q3;
            Q3=makeQuery(id+"F10.opExtrude","SWEPT_EDGE",EDGE,{"disambiguationData":[OSD([sQuery(id+"F9.wireOp",EDGE,"E5.4.2"),sQuery(id+"F9.wireOp",EDGE,"E5.4.3")])]});
            var Q4;
            Q4=makeQuery(id+"F10.opExtrude","CAP_EDGE",EDGE,{"disambiguationData":[OSD([sQuery(id+"F9.wireOp",EDGE,"E5.4.2")])],"isStart":false});
            var Q5;
            Q5=makeQuery(id+"F10.opExtrude","CAP_EDGE",EDGE,{"disambiguationData":[OSD([sQuery(id+"F9.wireOp",EDGE,"E5.4.0")])],"isStart":false});
            var Q6;
            Q6=makeQuery(id+"F10.opExtrude","CAP_EDGE",EDGE,{"disambiguationData":[OSD([sQuery(id+"F9.wireOp",EDGE,"E5.4.1")])],"isStart":false});
            var Q7;
            Q7=makeQuery(id+"F10.opExtrude","CAP_EDGE",EDGE,{"disambiguationData":[OSD([sQuery(id+"F9.wireOp",EDGE,"E5.4.3")])],"isStart":false});
            fillet(context, id + "F26", {"entities" : qUnion([Q0, Q1, Q2, Q3, Q4, Q5, Q6, Q7]), "radius" : 0.5 * mm, "tangentPropagation" : true, "allowEdgeOverflow" : false});
        }
        {
            var Q0;
            Q0=makeQuery(id+"F10.opExtrude","SWEPT_EDGE",EDGE,{"disambiguationData":[OSD([sQuery(id+"F9.wireOp",EDGE,"E5.3.0"),sQuery(id+"F9.wireOp",EDGE,"E5.3.1")])]});
            var Q1;
            Q1=makeQuery(id+"F10.opExtrude","SWEPT_EDGE",EDGE,{"disambiguationData":[OSD([sQuery(id+"F9.wireOp",EDGE,"E5.3.1"),sQuery(id+"F9.wireOp",EDGE,"E5.3.2")])]});
            var Q2;
            Q2=makeQuery(id+"F10.opExtrude","SWEPT_EDGE",EDGE,{"disambiguationData":[OSD([sQuery(id+"F9.wireOp",EDGE,"E5.3.0"),sQuery(id+"F9.wireOp",EDGE,"E5.3.3")])]});
            var Q3;
            Q3=makeQuery(id+"F10.opExtrude","SWEPT_EDGE",EDGE,{"disambiguationData":[OSD([sQuery(id+"F9.wireOp",EDGE,"E5.3.2"),sQuery(id+"F9.wireOp",EDGE,"E5.3.3")])]});
            var Q4;
            Q4=makeQuery(id+"F10.opExtrude","CAP_EDGE",EDGE,{"disambiguationData":[OSD([sQuery(id+"F9.wireOp",EDGE,"E5.3.2")])],"isStart":false});
            var Q5;
            Q5=makeQuery(id+"F10.opExtrude","CAP_EDGE",EDGE,{"disambiguationData":[OSD([sQuery(id+"F9.wireOp",EDGE,"E5.3.3")])],"isStart":false});
            var Q6;
            Q6=makeQuery(id+"F10.opExtrude","CAP_EDGE",EDGE,{"disambiguationData":[OSD([sQuery(id+"F9.wireOp",EDGE,"E5.3.0")])],"isStart":false});
            var Q7;
            Q7=makeQuery(id+"F10.opExtrude","CAP_EDGE",EDGE,{"disambiguationData":[OSD([sQuery(id+"F9.wireOp",EDGE,"E5.3.1")])],"isStart":false});
            fillet(context, id + "F27", {"entities" : qUnion([Q0, Q1, Q2, Q3, Q4, Q5, Q6, Q7]), "radius" : 0.5 * mm, "tangentPropagation" : true, "allowEdgeOverflow" : false});
        }
        {
            var Q0;
            Q0=makeQuery(id+"F10.opExtrude","SWEPT_EDGE",EDGE,{"disambiguationData":[OSD([sQuery(id+"F9.wireOp",EDGE,"E5.2.0"),sQuery(id+"F9.wireOp",EDGE,"E5.2.3")])]});
            var Q1;
            Q1=makeQuery(id+"F10.opExtrude","SWEPT_EDGE",EDGE,{"disambiguationData":[OSD([sQuery(id+"F9.wireOp",EDGE,"E5.2.2"),sQuery(id+"F9.wireOp",EDGE,"E5.2.3")])]});
            var Q2;
            Q2=makeQuery(id+"F10.opExtrude","SWEPT_EDGE",EDGE,{"disambiguationData":[OSD([sQuery(id+"F9.wireOp",EDGE,"E5.2.1"),sQuery(id+"F9.wireOp",EDGE,"E5.2.2")])]});
            var Q3;
            Q3=makeQuery(id+"F10.opExtrude","SWEPT_EDGE",EDGE,{"disambiguationData":[OSD([sQuery(id+"F9.wireOp",EDGE,"E5.2.0"),sQuery(id+"F9.wireOp",EDGE,"E5.2.1")])]});
            var Q4;
            Q4=makeQuery(id+"F10.opExtrude","CAP_EDGE",EDGE,{"disambiguationData":[OSD([sQuery(id+"F9.wireOp",EDGE,"E5.2.0")])],"isStart":false});
            var Q5;
            Q5=makeQuery(id+"F10.opExtrude","CAP_EDGE",EDGE,{"disambiguationData":[OSD([sQuery(id+"F9.wireOp",EDGE,"E5.2.2")])],"isStart":false});
            var Q6;
            Q6=makeQuery(id+"F10.opExtrude","CAP_EDGE",EDGE,{"disambiguationData":[OSD([sQuery(id+"F9.wireOp",EDGE,"E5.2.1")])],"isStart":false});
            var Q7;
            Q7=makeQuery(id+"F10.opExtrude","CAP_EDGE",EDGE,{"disambiguationData":[OSD([sQuery(id+"F9.wireOp",EDGE,"E5.2.3")])],"isStart":false});
            fillet(context, id + "F28", {"entities" : qUnion([Q0, Q1, Q2, Q3, Q4, Q5, Q6, Q7]), "radius" : 0.5 * mm, "tangentPropagation" : true, "allowEdgeOverflow" : false});
        }
        {
            var Q0;
            Q0=makeQuery(id+"F1.opExtrude","CAP_FACE",FACE,{"disambiguationData":[OSD([sQuery(id+"F0.wireOp",EDGE,"E0")])],"isStart":true});
            var sketch = newSketch(context, id + "F29", { "sketchPlane" : qUnion([Q0])});
            skCircle(sketch, "E6", {"center": v(0, 0) * mm, "radius": 9.26 * mm});
            skSolve(sketch);
        }
        {
            var Q0;
            Q0 = qSketchRegion(id + "F29", true);
            extrude(context, id + "F30", {"entities" : qUnion([Q0]), "operationType" : NewBodyOperationType.ADD, "depth" : 1.25 * mm, "offsetDistance" : 25 * mm});
        }
        {
            var Q0;
            Q0=makeQuery(id+"F30.opExtrude","CAP_FACE",FACE,{"disambiguationData":[OSD([sQuery(id+"F29.wireOp",EDGE,"E6")])],"isStart":false});
            var sketch = newSketch(context, id + "F31", { "sketchPlane" : qUnion([Q0])});
            skCircle(sketch, "E7", {"center": v(-4.5, 0) * mm, "radius": 0.75 * mm});
            skCircle(sketch, "E8", {"center": v(4.5, 0) * mm, "radius": 0.75 * mm});
            skSolve(sketch);
        }
        {
            var Q0;
            Q0 = qSketchRegion(id + "F31", true);
            extrude(context, id + "F32", {"entities" : qUnion([Q0]), "operationType" : NewBodyOperationType.ADD, "depth" : 1.5 * mm, "offsetDistance" : 25 * mm});
        }
        {
            var Q0;
            Q0=makeQuery(id+"F32.opExtrude","CAP_EDGE",EDGE,{"disambiguationData":[OSD([sQuery(id+"F31.wireOp",EDGE,"E7")])],"isStart":false});
            var Q1;
            Q1=makeQuery(id+"F32.opExtrude","CAP_EDGE",EDGE,{"disambiguationData":[OSD([sQuery(id+"F31.wireOp",EDGE,"E8")])],"isStart":false});
            chamfer(context, id + "F33", {"entities" : qUnion([Q0, Q1]), "width" : 0.2 * mm, "tangentPropagation" : true});
        }
        {
            var Q0;
            Q0=makeQuery(id+"F30.opExtrude","CAP_FACE",FACE,{"disambiguationData":[OSD([sQuery(id+"F29.wireOp",EDGE,"E6")])],"isStart":false});
            var sketch = newSketch(context, id + "F34", { "sketchPlane" : qUnion([Q0])});
            skLineSegment(sketch, "E9.bottom", {"start": v(-0.6, -9.16) * mm, "end": v(0.6, -9.16) * mm});
            skLineSegment(sketch, "E9.top", {"start": v(-0.6, -9.36) * mm, "end": v(0.6, -9.36) * mm});
            skLineSegment(sketch, "E9.left", {"start": v(-0.6, -9.16) * mm, "end": v(-0.6, -9.36) * mm});
            skLineSegment(sketch, "E9.right", {"start": v(0.6, -9.16) * mm, "end": v(0.6, -9.36) * mm});
            skLineSegment(sketch, "E10.bottom", {"start": v(-0.6, 1.47) * mm, "end": v(0.6, 1.47) * mm});
            skLineSegment(sketch, "E10.top", {"start": v(-0.6, 1.67) * mm, "end": v(0.6, 1.67) * mm});
            skLineSegment(sketch, "E10.left", {"start": v(-0.6, 1.47) * mm, "end": v(-0.6, 1.67) * mm});
            skLineSegment(sketch, "E10.right", {"start": v(0.6, 1.47) * mm, "end": v(0.6, 1.67) * mm});
            skLineSegment(sketch, "E11.bottom", {"start": v(-9.36, 0.6) * mm, "end": v(-9.16, 0.6) * mm});
            skLineSegment(sketch, "E11.top", {"start": v(-9.36, -0.6) * mm, "end": v(-9.16, -0.6) * mm});
            skLineSegment(sketch, "E11.left", {"start": v(-9.36, 0.6) * mm, "end": v(-9.36, -0.6) * mm});
            skLineSegment(sketch, "E11.right", {"start": v(-9.16, 0.6) * mm, "end": v(-9.16, -0.6) * mm});
            skLineSegment(sketch, "E12.bottom", {"start": v(9.16, 0.6) * mm, "end": v(9.36, 0.6) * mm});
            skLineSegment(sketch, "E12.top", {"start": v(9.16, -0.6) * mm, "end": v(9.36, -0.6) * mm});
            skLineSegment(sketch, "E12.left", {"start": v(9.16, 0.6) * mm, "end": v(9.16, -0.6) * mm});
            skLineSegment(sketch, "E12.right", {"start": v(9.36, 0.6) * mm, "end": v(9.36, -0.6) * mm});
            skSolve(sketch);
        }
        {
            var Q0;
            Q0 = qSketchRegion(id + "F34", true);
            extrude(context, id + "F35", {"entities" : qUnion([Q0]), "operationType" : NewBodyOperationType.ADD, "depth" : 3.5 * mm, "offsetDistance" : 25 * mm});
        }
        {
            var Q0;
            Q0=makeQuery(id+"F35.opExtrude","CAP_EDGE",EDGE,{"disambiguationData":[OSD([sQuery(id+"F34.wireOp",EDGE,"E10.right")])],"isStart":false});
            var Q1;
            Q1=makeQuery(id+"F35.opExtrude","CAP_EDGE",EDGE,{"disambiguationData":[OSD([sQuery(id+"F34.wireOp",EDGE,"E10.left")])],"isStart":false});
            var Q2;
            Q2=makeQuery(id+"F35.opExtrude","CAP_EDGE",EDGE,{"disambiguationData":[OSD([sQuery(id+"F34.wireOp",EDGE,"E9.left")])],"isStart":false});
            var Q3;
            Q3=makeQuery(id+"F35.opExtrude","CAP_EDGE",EDGE,{"disambiguationData":[OSD([sQuery(id+"F34.wireOp",EDGE,"E9.right")])],"isStart":false});
            var Q4;
            Q4=makeQuery(id+"F35.opExtrude","CAP_EDGE",EDGE,{"disambiguationData":[OSD([sQuery(id+"F34.wireOp",EDGE,"E12.bottom")])],"isStart":false});
            var Q5;
            Q5=makeQuery(id+"F35.opExtrude","CAP_EDGE",EDGE,{"disambiguationData":[OSD([sQuery(id+"F34.wireOp",EDGE,"E12.top")])],"isStart":false});
            var Q6;
            Q6=makeQuery(id+"F35.opExtrude","CAP_EDGE",EDGE,{"disambiguationData":[OSD([sQuery(id+"F34.wireOp",EDGE,"E11.top")])],"isStart":false});
            var Q7;
            Q7=makeQuery(id+"F35.opExtrude","CAP_EDGE",EDGE,{"disambiguationData":[OSD([sQuery(id+"F34.wireOp",EDGE,"E11.bottom")])],"isStart":false});
            fillet(context, id + "F36", {"entities" : qUnion([Q0, Q1, Q2, Q3, Q4, Q5, Q6, Q7]), "radius" : 0.6 * mm, "tangentPropagation" : true, "allowEdgeOverflow" : false});
        }
    });
